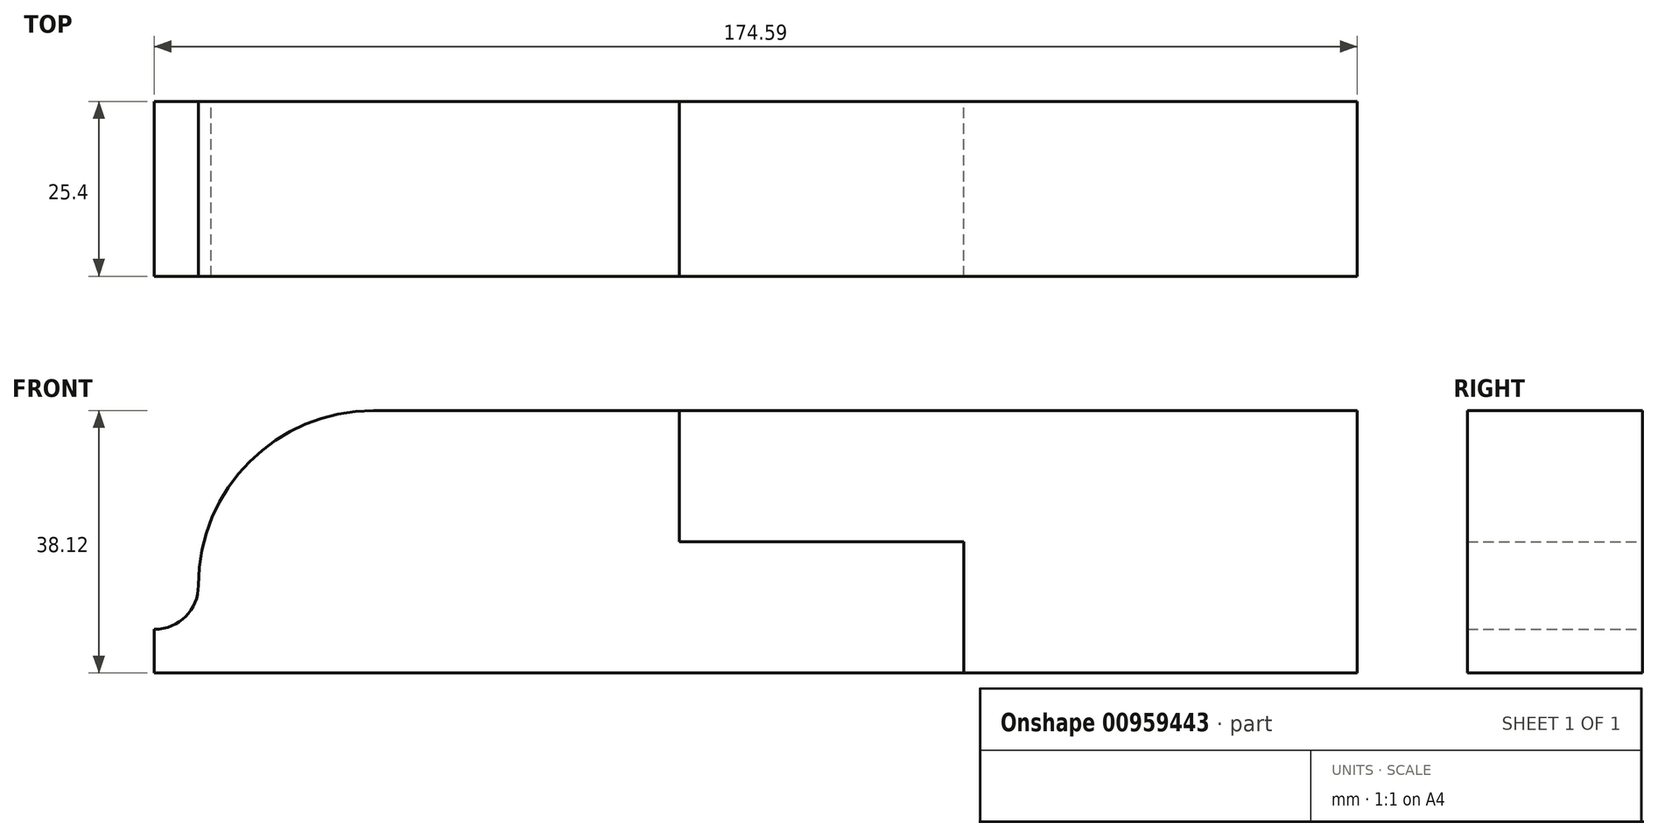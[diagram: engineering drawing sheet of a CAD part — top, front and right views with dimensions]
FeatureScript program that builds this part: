
annotation { "Feature Type Name" : "Feature", "Feature Type Description" : "" }
export const myFeature = defineFeature(function(context is Context, id is Id, definition is map)
    precondition{}
    {
        {
            var Q0;
            Q0=qCreatedBy(makeId("Front.planeOp"),FACE);
            var sketch = newSketch(context, id + "F0", { "sketchPlane" : qUnion([Q0])});
            skLineSegment(sketch, "E0", {"start": v(0, 0) * mm, "end": v(-44.66, 0) * mm});
            skLineSegment(sketch, "E1", {"start": v(-44.66, -0.02) * mm, "end": v(-44.66, 0) * mm});
            skLineSegment(sketch, "E2", {"start": v(-52.91, -0.02) * mm, "end": v(-44.66, -0.02) * mm});
            skLineSegment(sketch, "E3", {"start": v(-46.47, 12.68) * mm, "end": v(-46.47, 12.7) * mm});
            skLineSegment(sketch, "E4", {"start": v(-21.07, 38.1) * mm, "end": v(23.29, 38.1) * mm});
            skLineSegment(sketch, "E5", {"start": v(23.29, 38.1) * mm, "end": v(23.29, 19.05) * mm});
            skLineSegment(sketch, "E6", {"start": v(23.29, 19.05) * mm, "end": v(64.56, 19.05) * mm});
            skLineSegment(sketch, "E7", {"start": v(64.56, 19.05) * mm, "end": v(64.56, 0) * mm});
            skLineSegment(sketch, "E8", {"start": v(23.29, 38.1) * mm, "end": v(121.68, 38.1) * mm});
            skLineSegment(sketch, "E9", {"start": v(121.68, 38.1) * mm, "end": v(121.68, 0) * mm});
            skLineSegment(sketch, "E10", {"start": v(121.68, 0) * mm, "end": v(0, 0) * mm});
            skPoint(sketch, "E11.visualSharp", {"position": v(-46.47, 38.1) * mm});
            skArc(sketch, "E11.filletArc", {"start": v(-21.07, 38.1) * mm, "mid": v(-39.03, 30.66) * mm, "end": v(-46.47, 12.7) * mm});
            skPoint(sketch, "E12.visualSharp", {"position": v(-46.47, -0.02) * mm});
            skLineSegment(sketch, "E13", {"start": v(-52.82, 6.33) * mm, "end": v(-52.91, 6.33) * mm});
            skLineSegment(sketch, "E14", {"start": v(-52.91, 6.33) * mm, "end": v(-52.91, -0.02) * mm});
            skPoint(sketch, "E15.visualSharp", {"position": v(-46.47, 6.33) * mm});
            skArc(sketch, "E15.filletArc", {"start": v(-52.82, 6.33) * mm, "mid": v(-48.33, 8.2) * mm, "end": v(-46.47, 12.68) * mm});
            skSolve(sketch);
        }
        {
            var Q0;
            {var subQ2=sQuery(id+"F0.wireOp",EDGE,"E0");Q0=makeQuery(id+"F0.imprint","IMPRINT",FACE,{"disambiguationData":[TD([[makeQuery(id+"F0.imprint","IMPRINT",EDGE,{"derivedFrom":subQ2}),-1.0]])]});}
            extrude(context, id + "F1", {"entities" : qUnion([Q0]), "depth" : 25.4 * mm, "offsetDistance" : 25.4 * mm});
        }
        {
            var Q0;
            Q0=makeQuery(id+"F0.imprint","IMPRINT",FACE,{"disambiguationData":[TD([[makeQuery(id+"F0.imprint","IMPRINT",EDGE,{"derivedFrom":sQuery(id+"F0.wireOp",EDGE,"E5")}),1.0]])]});
            extrude(context, id + "F2", {"entities" : qUnion([Q0]), "depth" : 25.4 * mm, "offsetDistance" : 25.4 * mm});
        }
    });
